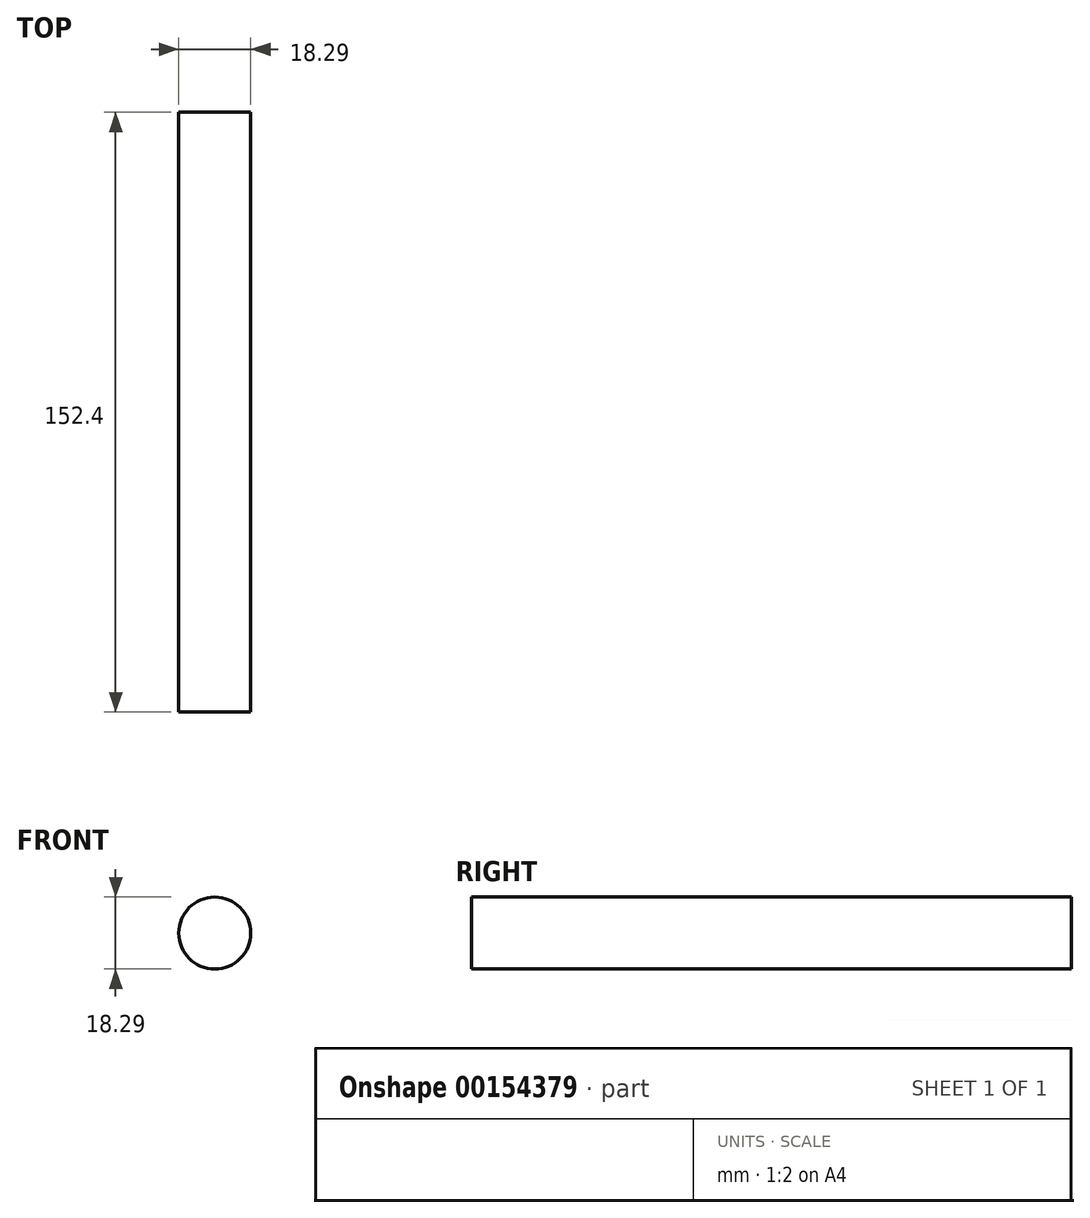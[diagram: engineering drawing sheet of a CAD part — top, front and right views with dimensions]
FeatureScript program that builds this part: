
annotation { "Feature Type Name" : "Feature", "Feature Type Description" : "" }
export const myFeature = defineFeature(function(context is Context, id is Id, definition is map)
    precondition{}
    {
        {
            var Q0;
            Q0=qCreatedBy(makeId("Front.planeOp"),FACE);
            var sketch = newSketch(context, id + "F0", { "sketchPlane" : qUnion([Q0])});
            skCircle(sketch, "E0", {"center": v(-59.85, 34.34) * mm, "radius": 9.14 * mm});
            skSolve(sketch);
        }
        {
            var Q0;
            Q0=makeQuery(id+"F0.imprint","IMPRINT",FACE,{"disambiguationData":[TD([[makeQuery(id+"F0.imprint","IMPRINT",EDGE,{"derivedFrom":sQuery(id+"F0.wireOp",EDGE,"E0")}),1.0]])]});
            extrude(context, id + "F1", {"entities" : qUnion([Q0]), "endBound" : BoundingType.SYMMETRIC, "depth" : 152.4 * mm});
        }
    });
